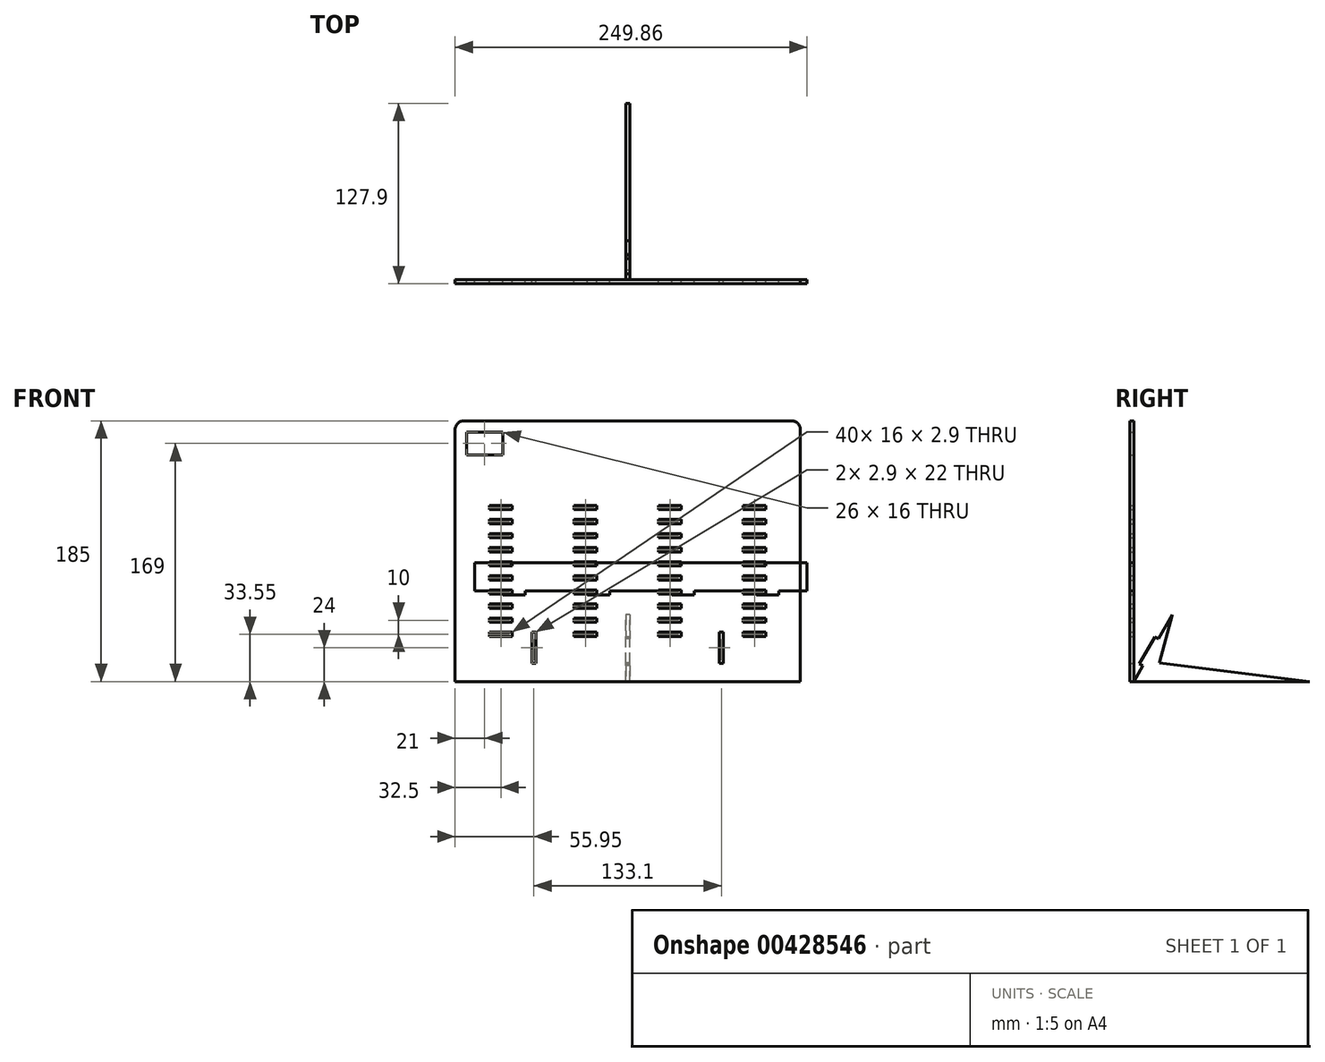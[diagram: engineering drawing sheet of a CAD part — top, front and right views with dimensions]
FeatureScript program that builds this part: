
annotation { "Feature Type Name" : "Feature", "Feature Type Description" : "" }
export const myFeature = defineFeature(function(context is Context, id is Id, definition is map)
    precondition{}
    {
        {
            var Q0;
            Q0=qCreatedBy(makeId("Front.planeOp"),FACE);
            var sketch = newSketch(context, id + "F0", { "sketchPlane" : qUnion([Q0])});
            skLineSegment(sketch, "E0.bottom", {"start": v(-116.5, 185) * mm, "end": v(116.5, 185) * mm});
            skLineSegment(sketch, "E0.top", {"start": v(-122.5, 0) * mm, "end": v(122.5, 0) * mm});
            skLineSegment(sketch, "E0.left", {"start": v(-122.5, 179) * mm, "end": v(-122.5, 0) * mm});
            skLineSegment(sketch, "E0.right", {"start": v(122.5, 179) * mm, "end": v(122.5, 0) * mm});
            skPoint(sketch, "E1", {"position": v(0, 0) * mm});
            skPoint(sketch, "E2.visualSharp", {"position": v(-122.5, 185) * mm});
            skArc(sketch, "E2.filletArc", {"start": v(-116.5, 185) * mm, "mid": v(-120.74, 183.24) * mm, "end": v(-122.5, 179) * mm});
            skPoint(sketch, "E3.visualSharp", {"position": v(122.5, 185) * mm});
            skArc(sketch, "E3.filletArc", {"start": v(122.5, 179) * mm, "mid": v(120.74, 183.24) * mm, "end": v(116.5, 185) * mm});
            skLineSegment(sketch, "E4.bottom", {"start": v(-114.5, 177) * mm, "end": v(-88.5, 177) * mm});
            skLineSegment(sketch, "E4.top", {"start": v(-114.5, 161) * mm, "end": v(-88.5, 161) * mm});
            skLineSegment(sketch, "E4.left", {"start": v(-114.5, 177) * mm, "end": v(-114.5, 161) * mm});
            skLineSegment(sketch, "E4.right", {"start": v(-88.5, 177) * mm, "end": v(-88.5, 161) * mm});
            skLineSegment(sketch, "E5.bottom", {"start": v(-98, 35) * mm, "end": v(-82, 35) * mm});
            skLineSegment(sketch, "E5.top", {"start": v(-98, 32.1) * mm, "end": v(-82, 32.1) * mm});
            skLineSegment(sketch, "E5.left", {"start": v(-98, 35) * mm, "end": v(-98, 32.1) * mm});
            skLineSegment(sketch, "E5.right", {"start": v(-82, 35) * mm, "end": v(-82, 32.1) * mm});
            skLineSegment(sketch, "E6.0.1.0", {"start": v(-98, 45) * mm, "end": v(-82, 45) * mm});
            skLineSegment(sketch, "E6.0.1.1", {"start": v(-98, 42.1) * mm, "end": v(-82, 42.1) * mm});
            skLineSegment(sketch, "E6.0.1.2", {"start": v(-82, 45) * mm, "end": v(-82, 42.1) * mm});
            skLineSegment(sketch, "E6.0.1.3", {"start": v(-98, 45) * mm, "end": v(-98, 42.1) * mm});
            skLineSegment(sketch, "E6.0.2.0", {"start": v(-98, 55) * mm, "end": v(-82, 55) * mm});
            skLineSegment(sketch, "E6.0.2.1", {"start": v(-98, 52.1) * mm, "end": v(-82, 52.1) * mm});
            skLineSegment(sketch, "E6.0.2.2", {"start": v(-82, 55) * mm, "end": v(-82, 52.1) * mm});
            skLineSegment(sketch, "E6.0.2.3", {"start": v(-98, 55) * mm, "end": v(-98, 52.1) * mm});
            skLineSegment(sketch, "E6.0.3.0", {"start": v(-98, 65) * mm, "end": v(-82, 65) * mm});
            skLineSegment(sketch, "E6.0.3.1", {"start": v(-98, 62.1) * mm, "end": v(-82, 62.1) * mm});
            skLineSegment(sketch, "E6.0.3.2", {"start": v(-82, 65) * mm, "end": v(-82, 62.1) * mm});
            skLineSegment(sketch, "E6.0.3.3", {"start": v(-98, 65) * mm, "end": v(-98, 62.1) * mm});
            skLineSegment(sketch, "E6.0.4.0", {"start": v(-98, 75) * mm, "end": v(-82, 75) * mm});
            skLineSegment(sketch, "E6.0.4.1", {"start": v(-98, 72.1) * mm, "end": v(-82, 72.1) * mm});
            skLineSegment(sketch, "E6.0.4.2", {"start": v(-82, 75) * mm, "end": v(-82, 72.1) * mm});
            skLineSegment(sketch, "E6.0.4.3", {"start": v(-98, 75) * mm, "end": v(-98, 72.1) * mm});
            skLineSegment(sketch, "E6.0.5.0", {"start": v(-98, 85) * mm, "end": v(-82, 85) * mm});
            skLineSegment(sketch, "E6.0.5.1", {"start": v(-98, 82.1) * mm, "end": v(-82, 82.1) * mm});
            skLineSegment(sketch, "E6.0.5.2", {"start": v(-82, 85) * mm, "end": v(-82, 82.1) * mm});
            skLineSegment(sketch, "E6.0.5.3", {"start": v(-98, 85) * mm, "end": v(-98, 82.1) * mm});
            skLineSegment(sketch, "E6.0.6.0", {"start": v(-98, 95) * mm, "end": v(-82, 95) * mm});
            skLineSegment(sketch, "E6.0.6.1", {"start": v(-98, 92.1) * mm, "end": v(-82, 92.1) * mm});
            skLineSegment(sketch, "E6.0.6.2", {"start": v(-82, 95) * mm, "end": v(-82, 92.1) * mm});
            skLineSegment(sketch, "E6.0.6.3", {"start": v(-98, 95) * mm, "end": v(-98, 92.1) * mm});
            skLineSegment(sketch, "E6.0.7.0", {"start": v(-98, 105) * mm, "end": v(-82, 105) * mm});
            skLineSegment(sketch, "E6.0.7.1", {"start": v(-98, 102.1) * mm, "end": v(-82, 102.1) * mm});
            skLineSegment(sketch, "E6.0.7.2", {"start": v(-82, 105) * mm, "end": v(-82, 102.1) * mm});
            skLineSegment(sketch, "E6.0.7.3", {"start": v(-98, 105) * mm, "end": v(-98, 102.1) * mm});
            skLineSegment(sketch, "E6.0.8.0", {"start": v(-98, 115) * mm, "end": v(-82, 115) * mm});
            skLineSegment(sketch, "E6.0.8.1", {"start": v(-98, 112.1) * mm, "end": v(-82, 112.1) * mm});
            skLineSegment(sketch, "E6.0.8.2", {"start": v(-82, 115) * mm, "end": v(-82, 112.1) * mm});
            skLineSegment(sketch, "E6.0.8.3", {"start": v(-98, 115) * mm, "end": v(-98, 112.1) * mm});
            skLineSegment(sketch, "E6.0.9.0", {"start": v(-98, 125) * mm, "end": v(-82, 125) * mm});
            skLineSegment(sketch, "E6.0.9.1", {"start": v(-98, 122.1) * mm, "end": v(-82, 122.1) * mm});
            skLineSegment(sketch, "E6.0.9.2", {"start": v(-82, 125) * mm, "end": v(-82, 122.1) * mm});
            skLineSegment(sketch, "E6.0.9.3", {"start": v(-98, 125) * mm, "end": v(-98, 122.1) * mm});
            skLineSegment(sketch, "E6.1.0.0", {"start": v(-38, 35) * mm, "end": v(-22, 35) * mm});
            skLineSegment(sketch, "E6.1.0.1", {"start": v(-38, 32.1) * mm, "end": v(-22, 32.1) * mm});
            skLineSegment(sketch, "E6.1.0.2", {"start": v(-22, 35) * mm, "end": v(-22, 32.1) * mm});
            skLineSegment(sketch, "E6.1.0.3", {"start": v(-38, 35) * mm, "end": v(-38, 32.1) * mm});
            skLineSegment(sketch, "E6.1.1.0", {"start": v(-38, 45) * mm, "end": v(-22, 45) * mm});
            skLineSegment(sketch, "E6.1.1.1", {"start": v(-38, 42.1) * mm, "end": v(-22, 42.1) * mm});
            skLineSegment(sketch, "E6.1.1.2", {"start": v(-22, 45) * mm, "end": v(-22, 42.1) * mm});
            skLineSegment(sketch, "E6.1.1.3", {"start": v(-38, 45) * mm, "end": v(-38, 42.1) * mm});
            skLineSegment(sketch, "E6.1.2.0", {"start": v(-38, 55) * mm, "end": v(-22, 55) * mm});
            skLineSegment(sketch, "E6.1.2.1", {"start": v(-38, 52.1) * mm, "end": v(-22, 52.1) * mm});
            skLineSegment(sketch, "E6.1.2.2", {"start": v(-22, 55) * mm, "end": v(-22, 52.1) * mm});
            skLineSegment(sketch, "E6.1.2.3", {"start": v(-38, 55) * mm, "end": v(-38, 52.1) * mm});
            skLineSegment(sketch, "E6.1.3.0", {"start": v(-38, 65) * mm, "end": v(-22, 65) * mm});
            skLineSegment(sketch, "E6.1.3.1", {"start": v(-38, 62.1) * mm, "end": v(-22, 62.1) * mm});
            skLineSegment(sketch, "E6.1.3.2", {"start": v(-22, 65) * mm, "end": v(-22, 62.1) * mm});
            skLineSegment(sketch, "E6.1.3.3", {"start": v(-38, 65) * mm, "end": v(-38, 62.1) * mm});
            skLineSegment(sketch, "E6.1.4.0", {"start": v(-38, 75) * mm, "end": v(-22, 75) * mm});
            skLineSegment(sketch, "E6.1.4.1", {"start": v(-38, 72.1) * mm, "end": v(-22, 72.1) * mm});
            skLineSegment(sketch, "E6.1.4.2", {"start": v(-22, 75) * mm, "end": v(-22, 72.1) * mm});
            skLineSegment(sketch, "E6.1.4.3", {"start": v(-38, 75) * mm, "end": v(-38, 72.1) * mm});
            skLineSegment(sketch, "E6.1.5.0", {"start": v(-38, 85) * mm, "end": v(-22, 85) * mm});
            skLineSegment(sketch, "E6.1.5.1", {"start": v(-38, 82.1) * mm, "end": v(-22, 82.1) * mm});
            skLineSegment(sketch, "E6.1.5.2", {"start": v(-22, 85) * mm, "end": v(-22, 82.1) * mm});
            skLineSegment(sketch, "E6.1.5.3", {"start": v(-38, 85) * mm, "end": v(-38, 82.1) * mm});
            skLineSegment(sketch, "E6.1.6.0", {"start": v(-38, 95) * mm, "end": v(-22, 95) * mm});
            skLineSegment(sketch, "E6.1.6.1", {"start": v(-38, 92.1) * mm, "end": v(-22, 92.1) * mm});
            skLineSegment(sketch, "E6.1.6.2", {"start": v(-22, 95) * mm, "end": v(-22, 92.1) * mm});
            skLineSegment(sketch, "E6.1.6.3", {"start": v(-38, 95) * mm, "end": v(-38, 92.1) * mm});
            skLineSegment(sketch, "E6.1.7.0", {"start": v(-38, 105) * mm, "end": v(-22, 105) * mm});
            skLineSegment(sketch, "E6.1.7.1", {"start": v(-38, 102.1) * mm, "end": v(-22, 102.1) * mm});
            skLineSegment(sketch, "E6.1.7.2", {"start": v(-22, 105) * mm, "end": v(-22, 102.1) * mm});
            skLineSegment(sketch, "E6.1.7.3", {"start": v(-38, 105) * mm, "end": v(-38, 102.1) * mm});
            skLineSegment(sketch, "E6.1.8.0", {"start": v(-38, 115) * mm, "end": v(-22, 115) * mm});
            skLineSegment(sketch, "E6.1.8.1", {"start": v(-38, 112.1) * mm, "end": v(-22, 112.1) * mm});
            skLineSegment(sketch, "E6.1.8.2", {"start": v(-22, 115) * mm, "end": v(-22, 112.1) * mm});
            skLineSegment(sketch, "E6.1.8.3", {"start": v(-38, 115) * mm, "end": v(-38, 112.1) * mm});
            skLineSegment(sketch, "E6.1.9.0", {"start": v(-38, 125) * mm, "end": v(-22, 125) * mm});
            skLineSegment(sketch, "E6.1.9.1", {"start": v(-38, 122.1) * mm, "end": v(-22, 122.1) * mm});
            skLineSegment(sketch, "E6.1.9.2", {"start": v(-22, 125) * mm, "end": v(-22, 122.1) * mm});
            skLineSegment(sketch, "E6.1.9.3", {"start": v(-38, 125) * mm, "end": v(-38, 122.1) * mm});
            skLineSegment(sketch, "E6.2.0.0", {"start": v(22, 35) * mm, "end": v(38, 35) * mm});
            skLineSegment(sketch, "E6.2.0.1", {"start": v(22, 32.1) * mm, "end": v(38, 32.1) * mm});
            skLineSegment(sketch, "E6.2.0.2", {"start": v(38, 35) * mm, "end": v(38, 32.1) * mm});
            skLineSegment(sketch, "E6.2.0.3", {"start": v(22, 35) * mm, "end": v(22, 32.1) * mm});
            skLineSegment(sketch, "E6.2.1.0", {"start": v(22, 45) * mm, "end": v(38, 45) * mm});
            skLineSegment(sketch, "E6.2.1.1", {"start": v(22, 42.1) * mm, "end": v(38, 42.1) * mm});
            skLineSegment(sketch, "E6.2.1.2", {"start": v(38, 45) * mm, "end": v(38, 42.1) * mm});
            skLineSegment(sketch, "E6.2.1.3", {"start": v(22, 45) * mm, "end": v(22, 42.1) * mm});
            skLineSegment(sketch, "E6.2.2.0", {"start": v(22, 55) * mm, "end": v(38, 55) * mm});
            skLineSegment(sketch, "E6.2.2.1", {"start": v(22, 52.1) * mm, "end": v(38, 52.1) * mm});
            skLineSegment(sketch, "E6.2.2.2", {"start": v(38, 55) * mm, "end": v(38, 52.1) * mm});
            skLineSegment(sketch, "E6.2.2.3", {"start": v(22, 55) * mm, "end": v(22, 52.1) * mm});
            skLineSegment(sketch, "E6.2.3.0", {"start": v(22, 65) * mm, "end": v(38, 65) * mm});
            skLineSegment(sketch, "E6.2.3.1", {"start": v(22, 62.1) * mm, "end": v(38, 62.1) * mm});
            skLineSegment(sketch, "E6.2.3.2", {"start": v(38, 65) * mm, "end": v(38, 62.1) * mm});
            skLineSegment(sketch, "E6.2.3.3", {"start": v(22, 65) * mm, "end": v(22, 62.1) * mm});
            skLineSegment(sketch, "E6.2.4.0", {"start": v(22, 75) * mm, "end": v(38, 75) * mm});
            skLineSegment(sketch, "E6.2.4.1", {"start": v(22, 72.1) * mm, "end": v(38, 72.1) * mm});
            skLineSegment(sketch, "E6.2.4.2", {"start": v(38, 75) * mm, "end": v(38, 72.1) * mm});
            skLineSegment(sketch, "E6.2.4.3", {"start": v(22, 75) * mm, "end": v(22, 72.1) * mm});
            skLineSegment(sketch, "E6.2.5.0", {"start": v(22, 85) * mm, "end": v(38, 85) * mm});
            skLineSegment(sketch, "E6.2.5.1", {"start": v(22, 82.1) * mm, "end": v(38, 82.1) * mm});
            skLineSegment(sketch, "E6.2.5.2", {"start": v(38, 85) * mm, "end": v(38, 82.1) * mm});
            skLineSegment(sketch, "E6.2.5.3", {"start": v(22, 85) * mm, "end": v(22, 82.1) * mm});
            skLineSegment(sketch, "E6.2.6.0", {"start": v(22, 95) * mm, "end": v(38, 95) * mm});
            skLineSegment(sketch, "E6.2.6.1", {"start": v(22, 92.1) * mm, "end": v(38, 92.1) * mm});
            skLineSegment(sketch, "E6.2.6.2", {"start": v(38, 95) * mm, "end": v(38, 92.1) * mm});
            skLineSegment(sketch, "E6.2.6.3", {"start": v(22, 95) * mm, "end": v(22, 92.1) * mm});
            skLineSegment(sketch, "E6.2.7.0", {"start": v(22, 105) * mm, "end": v(38, 105) * mm});
            skLineSegment(sketch, "E6.2.7.1", {"start": v(22, 102.1) * mm, "end": v(38, 102.1) * mm});
            skLineSegment(sketch, "E6.2.7.2", {"start": v(38, 105) * mm, "end": v(38, 102.1) * mm});
            skLineSegment(sketch, "E6.2.7.3", {"start": v(22, 105) * mm, "end": v(22, 102.1) * mm});
            skLineSegment(sketch, "E6.2.8.0", {"start": v(22, 115) * mm, "end": v(38, 115) * mm});
            skLineSegment(sketch, "E6.2.8.1", {"start": v(22, 112.1) * mm, "end": v(38, 112.1) * mm});
            skLineSegment(sketch, "E6.2.8.2", {"start": v(38, 115) * mm, "end": v(38, 112.1) * mm});
            skLineSegment(sketch, "E6.2.8.3", {"start": v(22, 115) * mm, "end": v(22, 112.1) * mm});
            skLineSegment(sketch, "E6.2.9.0", {"start": v(22, 125) * mm, "end": v(38, 125) * mm});
            skLineSegment(sketch, "E6.2.9.1", {"start": v(22, 122.1) * mm, "end": v(38, 122.1) * mm});
            skLineSegment(sketch, "E6.2.9.2", {"start": v(38, 125) * mm, "end": v(38, 122.1) * mm});
            skLineSegment(sketch, "E6.2.9.3", {"start": v(22, 125) * mm, "end": v(22, 122.1) * mm});
            skLineSegment(sketch, "E6.3.0.0", {"start": v(82, 35) * mm, "end": v(98, 35) * mm});
            skLineSegment(sketch, "E6.3.0.1", {"start": v(82, 32.1) * mm, "end": v(98, 32.1) * mm});
            skLineSegment(sketch, "E6.3.0.2", {"start": v(98, 35) * mm, "end": v(98, 32.1) * mm});
            skLineSegment(sketch, "E6.3.0.3", {"start": v(82, 35) * mm, "end": v(82, 32.1) * mm});
            skLineSegment(sketch, "E6.3.1.0", {"start": v(82, 45) * mm, "end": v(98, 45) * mm});
            skLineSegment(sketch, "E6.3.1.1", {"start": v(82, 42.1) * mm, "end": v(98, 42.1) * mm});
            skLineSegment(sketch, "E6.3.1.2", {"start": v(98, 45) * mm, "end": v(98, 42.1) * mm});
            skLineSegment(sketch, "E6.3.1.3", {"start": v(82, 45) * mm, "end": v(82, 42.1) * mm});
            skLineSegment(sketch, "E6.3.2.0", {"start": v(82, 55) * mm, "end": v(98, 55) * mm});
            skLineSegment(sketch, "E6.3.2.1", {"start": v(82, 52.1) * mm, "end": v(98, 52.1) * mm});
            skLineSegment(sketch, "E6.3.2.2", {"start": v(98, 55) * mm, "end": v(98, 52.1) * mm});
            skLineSegment(sketch, "E6.3.2.3", {"start": v(82, 55) * mm, "end": v(82, 52.1) * mm});
            skLineSegment(sketch, "E6.3.3.0", {"start": v(82, 65) * mm, "end": v(98, 65) * mm});
            skLineSegment(sketch, "E6.3.3.1", {"start": v(82, 62.1) * mm, "end": v(98, 62.1) * mm});
            skLineSegment(sketch, "E6.3.3.2", {"start": v(98, 65) * mm, "end": v(98, 62.1) * mm});
            skLineSegment(sketch, "E6.3.3.3", {"start": v(82, 65) * mm, "end": v(82, 62.1) * mm});
            skLineSegment(sketch, "E6.3.4.0", {"start": v(82, 75) * mm, "end": v(98, 75) * mm});
            skLineSegment(sketch, "E6.3.4.1", {"start": v(82, 72.1) * mm, "end": v(98, 72.1) * mm});
            skLineSegment(sketch, "E6.3.4.2", {"start": v(98, 75) * mm, "end": v(98, 72.1) * mm});
            skLineSegment(sketch, "E6.3.4.3", {"start": v(82, 75) * mm, "end": v(82, 72.1) * mm});
            skLineSegment(sketch, "E6.3.5.0", {"start": v(82, 85) * mm, "end": v(98, 85) * mm});
            skLineSegment(sketch, "E6.3.5.1", {"start": v(82, 82.1) * mm, "end": v(98, 82.1) * mm});
            skLineSegment(sketch, "E6.3.5.2", {"start": v(98, 85) * mm, "end": v(98, 82.1) * mm});
            skLineSegment(sketch, "E6.3.5.3", {"start": v(82, 85) * mm, "end": v(82, 82.1) * mm});
            skLineSegment(sketch, "E6.3.6.0", {"start": v(82, 95) * mm, "end": v(98, 95) * mm});
            skLineSegment(sketch, "E6.3.6.1", {"start": v(82, 92.1) * mm, "end": v(98, 92.1) * mm});
            skLineSegment(sketch, "E6.3.6.2", {"start": v(98, 95) * mm, "end": v(98, 92.1) * mm});
            skLineSegment(sketch, "E6.3.6.3", {"start": v(82, 95) * mm, "end": v(82, 92.1) * mm});
            skLineSegment(sketch, "E6.3.7.0", {"start": v(82, 105) * mm, "end": v(98, 105) * mm});
            skLineSegment(sketch, "E6.3.7.1", {"start": v(82, 102.1) * mm, "end": v(98, 102.1) * mm});
            skLineSegment(sketch, "E6.3.7.2", {"start": v(98, 105) * mm, "end": v(98, 102.1) * mm});
            skLineSegment(sketch, "E6.3.7.3", {"start": v(82, 105) * mm, "end": v(82, 102.1) * mm});
            skLineSegment(sketch, "E6.3.8.0", {"start": v(82, 115) * mm, "end": v(98, 115) * mm});
            skLineSegment(sketch, "E6.3.8.1", {"start": v(82, 112.1) * mm, "end": v(98, 112.1) * mm});
            skLineSegment(sketch, "E6.3.8.2", {"start": v(98, 115) * mm, "end": v(98, 112.1) * mm});
            skLineSegment(sketch, "E6.3.8.3", {"start": v(82, 115) * mm, "end": v(82, 112.1) * mm});
            skLineSegment(sketch, "E6.3.9.0", {"start": v(82, 125) * mm, "end": v(98, 125) * mm});
            skLineSegment(sketch, "E6.3.9.1", {"start": v(82, 122.1) * mm, "end": v(98, 122.1) * mm});
            skLineSegment(sketch, "E6.3.9.2", {"start": v(98, 125) * mm, "end": v(98, 122.1) * mm});
            skLineSegment(sketch, "E6.3.9.3", {"start": v(82, 125) * mm, "end": v(82, 122.1) * mm});
            skLineSegment(sketch, "E6.direction1", {"start": v(-98, 35) * mm, "end": v(-38, 35) * mm, "construction": true});
            skLineSegment(sketch, "E6.direction2", {"start": v(-98, 35) * mm, "end": v(-98, 45) * mm, "construction": true});
            skLineSegment(sketch, "E7", {"start": v(-22, 125) * mm, "end": v(22, 125) * mm, "construction": true});
            skLineSegment(sketch, "E8", {"start": v(0, 0) * mm, "end": v(0, 185) * mm, "construction": true});
            skPoint(sketch, "E9", {"position": v(0, 125) * mm});
            skLineSegment(sketch, "E10.bottom", {"start": v(-68, 35) * mm, "end": v(-65.1, 35) * mm});
            skLineSegment(sketch, "E10.top", {"start": v(-68, 13) * mm, "end": v(-65.1, 13) * mm});
            skLineSegment(sketch, "E10.left", {"start": v(-68, 35) * mm, "end": v(-68, 13) * mm});
            skLineSegment(sketch, "E10.right", {"start": v(-65.1, 35) * mm, "end": v(-65.1, 13) * mm});
            skLineSegment(sketch, "E11.MirrorCS", {"start": v(68, 35) * mm, "end": v(65.1, 35) * mm});
            skLineSegment(sketch, "E12.MirrorCS", {"start": v(65.1, 35) * mm, "end": v(65.1, 13) * mm});
            skLineSegment(sketch, "E13.MirrorCS", {"start": v(68, 35) * mm, "end": v(68, 13) * mm});
            skLineSegment(sketch, "E14.MirrorCS", {"start": v(68, 13) * mm, "end": v(65.1, 13) * mm});
            skSolve(sketch);
        }
        {
            var Q0;
            Q0=makeQuery(id+"F0.imprint","IMPRINT",FACE,{"disambiguationData":[TD([[makeQuery(id+"F0.imprint","IMPRINT",EDGE,{"derivedFrom":sQuery(id+"F0.wireOp",EDGE,"E0.bottom")}),-1.0]])]});
            extrude(context, id + "F1", {"entities" : qUnion([Q0]), "depth" : 2.9 * mm});
        }
        {
            var Q0;
            Q0=qCreatedBy(makeId("Right.planeOp"),FACE);
            var sketch = newSketch(context, id + "F2", { "sketchPlane" : qUnion([Q0])});
            skLineSegment(sketch, "E15", {"start": v(0, 0) * mm, "end": v(125, 0) * mm});
            skLineSegment(sketch, "E16", {"start": v(125, 0) * mm, "end": v(18.25, 13.1) * mm});
            skLineSegment(sketch, "E17", {"start": v(18.25, 13.1) * mm, "end": v(27.5, 47.63) * mm});
            skLineSegment(sketch, "E18", {"start": v(27.5, 47.63) * mm, "end": v(17.5, 30.31) * mm});
            skLineSegment(sketch, "E19", {"start": v(6.5, 11.26) * mm, "end": v(6.5, 11.26) * mm});
            skLineSegment(sketch, "E20", {"start": v(3.99, 12.7) * mm, "end": v(14.99, 31.76) * mm});
            skLineSegment(sketch, "E21", {"start": v(14.99, 31.76) * mm, "end": v(17.5, 30.31) * mm});
            skLineSegment(sketch, "E22", {"start": v(6.5, 11.26) * mm, "end": v(3.99, 12.7) * mm});
            skLineSegment(sketch, "E23", {"start": v(6.5, 11.26) * mm, "end": v(0, 0) * mm});
            skSolve(sketch);
        }
        {
            var Q0;
            {var subQ0=sQuery(id+"F2.wireOp",EDGE,"E19");Q0=makeQuery(id+"F2.imprint","IMPRINT",FACE,{"disambiguationData":[TD([[makeQuery(id+"F2.imprint","IMPRINT",EDGE,{"derivedFrom":subQ0}),-1.0]])]});}
            var Q1;
            {var subQ3=sQuery(id+"F2.wireOp",EDGE,"E15");Q1=makeQuery(id+"F2.imprint","IMPRINT",FACE,{"disambiguationData":[TD([[makeQuery(id+"F2.imprint","IMPRINT",EDGE,{"derivedFrom":subQ3}),1.0]])]});}
            extrude(context, id + "F3", {"entities" : qUnion([Q0, Q1]), "endBound" : BoundingType.SYMMETRIC, "depth" : 2.9 * mm});
        }
        {
            var Q0;
            Q0=qCreatedBy(makeId("Front.planeOp"),FACE);
            var sketch = newSketch(context, id + "F4", { "sketchPlane" : qUnion([Q0])});
            skLineSegment(sketch, "E24", {"start": v(-108.64, 64.3) * mm, "end": v(-88.64, 64.3) * mm});
            skLineSegment(sketch, "E25", {"start": v(-88.64, 64.3) * mm, "end": v(-88.64, 61.4) * mm});
            skLineSegment(sketch, "E26", {"start": v(-88.64, 61.4) * mm, "end": v(-72.64, 61.4) * mm});
            skLineSegment(sketch, "E27", {"start": v(-72.64, 61.4) * mm, "end": v(-72.64, 64.3) * mm});
            skLineSegment(sketch, "E28", {"start": v(-72.64, 64.3) * mm, "end": v(-28.64, 64.3) * mm});
            skLineSegment(sketch, "E29", {"start": v(-28.64, 64.3) * mm, "end": v(-28.64, 61.4) * mm});
            skLineSegment(sketch, "E30", {"start": v(-28.64, 61.4) * mm, "end": v(-12.64, 61.4) * mm});
            skLineSegment(sketch, "E31", {"start": v(-12.64, 61.4) * mm, "end": v(-12.64, 64.3) * mm});
            skLineSegment(sketch, "E32", {"start": v(-12.64, 64.3) * mm, "end": v(31.36, 64.3) * mm});
            skLineSegment(sketch, "E33", {"start": v(31.36, 64.3) * mm, "end": v(31.36, 61.4) * mm});
            skLineSegment(sketch, "E34", {"start": v(31.36, 61.4) * mm, "end": v(47.36, 61.4) * mm});
            skLineSegment(sketch, "E35", {"start": v(47.36, 61.4) * mm, "end": v(47.36, 64.3) * mm});
            skLineSegment(sketch, "E36", {"start": v(47.36, 64.3) * mm, "end": v(91.36, 64.3) * mm});
            skLineSegment(sketch, "E37", {"start": v(91.36, 64.3) * mm, "end": v(91.36, 61.4) * mm});
            skLineSegment(sketch, "E38", {"start": v(91.36, 61.4) * mm, "end": v(107.36, 61.4) * mm});
            skLineSegment(sketch, "E39", {"start": v(107.36, 61.4) * mm, "end": v(107.36, 64.3) * mm});
            skLineSegment(sketch, "E40", {"start": v(107.36, 64.3) * mm, "end": v(127.36, 64.3) * mm});
            skLineSegment(sketch, "E41", {"start": v(127.36, 64.3) * mm, "end": v(127.36, 84.3) * mm});
            skLineSegment(sketch, "E42", {"start": v(127.36, 84.3) * mm, "end": v(-108.64, 84.3) * mm});
            skLineSegment(sketch, "E43", {"start": v(-108.64, 84.3) * mm, "end": v(-108.64, 64.3) * mm});
            skSolve(sketch);
        }
        {
            var Q0;
            Q0=makeQuery(id+"F4.imprint","IMPRINT",FACE,{"disambiguationData":[TD([[makeQuery(id+"F4.imprint","IMPRINT",EDGE,{"derivedFrom":sQuery(id+"F4.wireOp",EDGE,"E24")}),1.0]])]});
            extrude(context, id + "F5", {"entities" : qUnion([Q0]), "depth" : 2.9 * mm});
        }
    });
